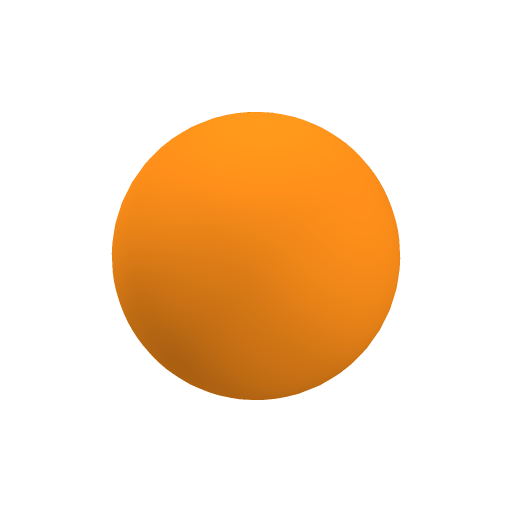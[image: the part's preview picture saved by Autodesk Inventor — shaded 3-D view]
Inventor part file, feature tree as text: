
AUTODESK INVENTOR PART (.ipt)
format: ipt  version: 2023 (Build 270158000, 158)  size: 130,048 bytes
history: native  units: mm
features: revolve x1, sketch x1
ambient origin geometry x8: Origin, YZ Plane, XZ Plane, XY Plane, X Axis, Y Axis, Z Axis, Center Point
bodies: Solid1 (feature_tree)
feature tree (2):
  revolve  "Revolution1"  Angle=90.0deg
  sketch  "Sketch1"  dims[d0=17.0mm d1=90.0deg]
